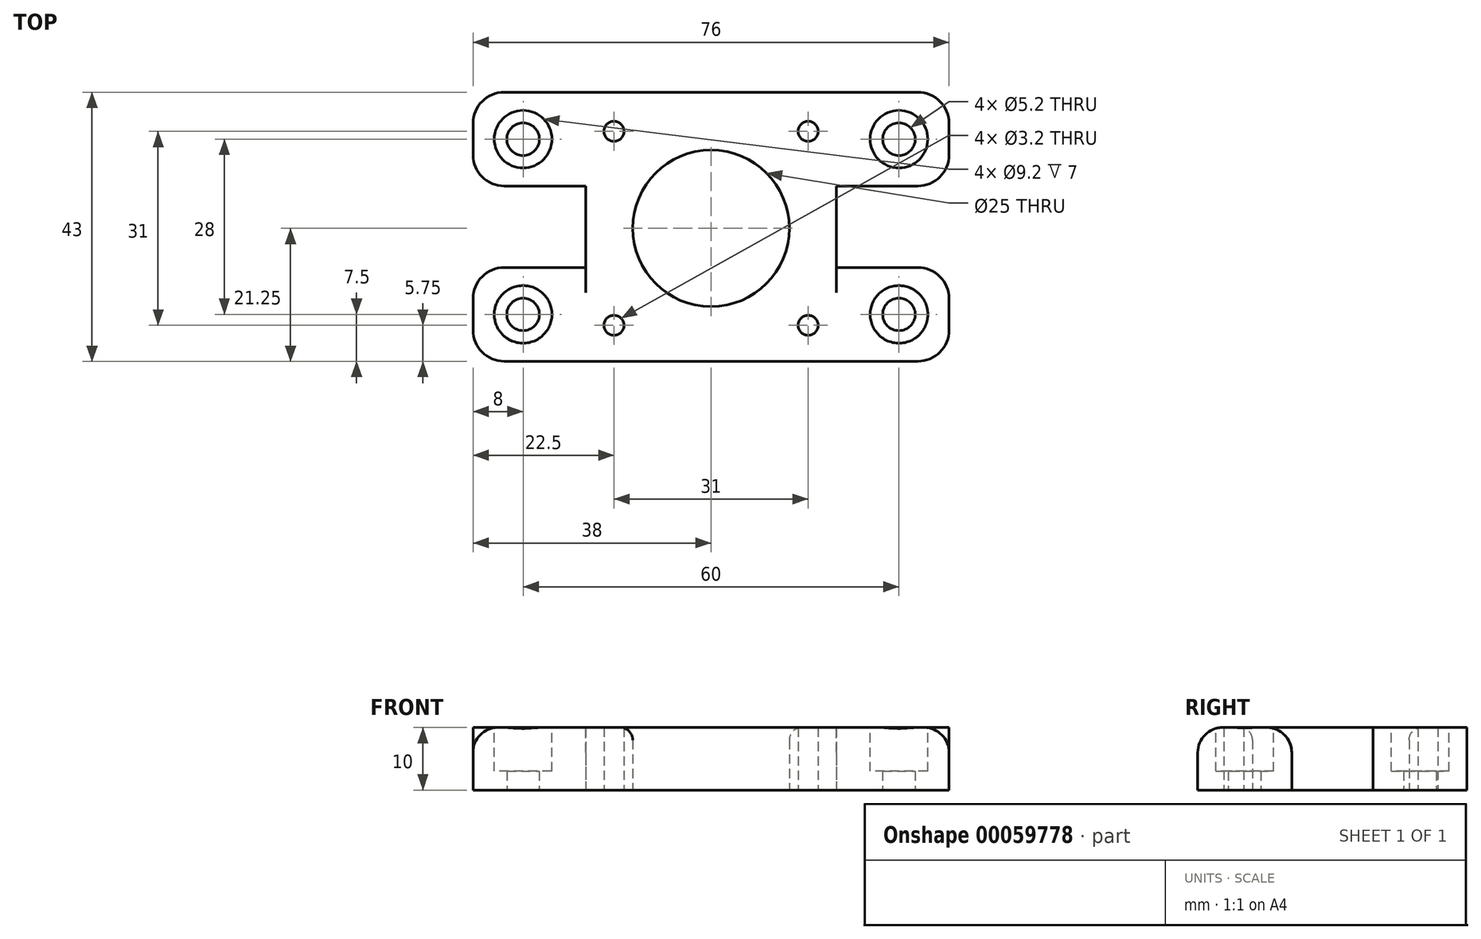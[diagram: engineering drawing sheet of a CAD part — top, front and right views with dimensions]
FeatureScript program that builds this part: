
annotation { "Feature Type Name" : "Feature", "Feature Type Description" : "" }
export const myFeature = defineFeature(function(context is Context, id is Id, definition is map)
    precondition{}
    {
        {
            assignVariable(context, id + "F0", {"name" : "defaultThickness", "anyValue" : 10 * mm});
        }
        {
            var Q0;
            Q0=qCreatedBy(makeId("Top.planeOp"),FACE);
            var sketch = newSketch(context, id + "F1", { "sketchPlane" : qUnion([Q0])});
            skLineSegment(sketch, "E0.rect.bottom", {"start": v(-20, 21.5) * mm, "end": v(20, 21.5) * mm});
            skLineSegment(sketch, "E0.rect.top", {"start": v(-20, -21.5) * mm, "end": v(20, -21.5) * mm});
            skLineSegment(sketch, "E0.rect.left", {"start": v(-20, 21.5) * mm, "end": v(-20, -21.5) * mm});
            skLineSegment(sketch, "E0.rect.right", {"start": v(20, 21.5) * mm, "end": v(20, -21.5) * mm});
            skPoint(sketch, "E0.rect.middle", {"position": v(0, 0) * mm});
            skLineSegment(sketch, "E1", {"start": v(0, 21.5) * mm, "end": v(0, 0) * mm, "construction": true});
            skLineSegment(sketch, "E2", {"start": v(0, -21.5) * mm, "end": v(0, 0) * mm, "construction": true});
            skSolve(sketch);
        }
        {
            var Q0;
            Q0=qSketchRegion(id+"F1",true);
            extrude(context, id + "F2", {"entities" : qUnion([Q0]), "depth" : getVariable(context, 'defaultThickness')});
        }
        {
            var Q0;
            Q0=makeQuery(id+"F2.opExtrude","CAP_FACE",FACE,{"disambiguationData":[OSD([sQuery(id+"F1.wireOp",EDGE,"E0.rect.bottom"),sQuery(id+"F1.wireOp",EDGE,"E0.rect.top"),sQuery(id+"F1.wireOp",EDGE,"E0.rect.left"),sQuery(id+"F1.wireOp",EDGE,"E0.rect.right"),sQuery(id+"F1.wireOp",EDGE,"f753b575-aba3-41a6-833e-e4f93ea5e4c448.MirrorCS"),sQuery(id+"F1.wireOp",EDGE,"f753b575-aba3-41a6-833e-e4f93ea5e4c449.MirrorC"),sQuery(id+"F1.wireOp",EDGE,"f753b575-aba3-41a6-833e-e4f93ea5e4c450.MirrorCS"),sQuery(id+"F1.wireOp",EDGE,"f753b575-aba3-41a6-833e-e4f93ea5e4c451.MirrorCS"),sQuery(id+"F1.wireOp",EDGE,"bc571038-01dd-487e-b9a0-def5901bd9830.MirrorCS"),sQuery(id+"F1.wireOp",EDGE,"12bf195a-cfe4-4b15-ab7f-3f731c2d51660.MirrorCS"),sQuery(id+"F1.wireOp",EDGE,"455051b4-7426-46a8-a129-8b9c592178470.MirrorCS"),sQuery(id+"F1.wireOp",EDGE,"7dd5bb44-a427-4bdb-ba85-5ced25b216bb0.MirrorC")])],"isStart":true});
            var sketch = newSketch(context, id + "F3", { "sketchPlane" : qUnion([Q0])});
            skLineSegment(sketch, "E3", {"start": v(20, -21.5) * mm, "end": v(20, -21.5) * mm});
            skLineSegment(sketch, "E4", {"start": v(20, -21.5) * mm, "end": v(-20, -21.5) * mm, "construction": true});
            skLineSegment(sketch, "E5", {"start": v(-20, -21.5) * mm, "end": v(-20, -21.5) * mm});
            skLineSegment(sketch, "E6", {"start": v(0, 21.5) * mm, "end": v(0, 0) * mm, "construction": true});
            skLineSegment(sketch, "E7", {"start": v(0, 0) * mm, "end": v(0, -21) * mm, "construction": true});
            skLineSegment(sketch, "E8", {"start": v(0, -21) * mm, "end": v(-20, -21) * mm, "construction": true});
            skLineSegment(sketch, "E9", {"start": v(-20, -21) * mm, "end": v(-20, 21.5) * mm, "construction": true});
            skLineSegment(sketch, "E10", {"start": v(-20, 21.5) * mm, "end": v(0, 21.5) * mm, "construction": true});
            skLineSegment(sketch, "E11", {"start": v(20, 21.5) * mm, "end": v(20, -21) * mm, "construction": true});
            skLineSegment(sketch, "E12", {"start": v(20, -21) * mm, "end": v(0, -21) * mm, "construction": true});
            skLineSegment(sketch, "E13", {"start": v(-20, 0.25) * mm, "end": v(0, 0.25) * mm, "construction": true});
            skLineSegment(sketch, "E14", {"start": v(0, 0.25) * mm, "end": v(20, 0.25) * mm, "construction": true});
            skPoint(sketch, "E15", {"position": v(0, 0.25) * mm});
            skCircle(sketch, "E16", {"center": v(0, 0.25) * mm, "radius": 12.5 * mm});
            skCircle(sketch, "E17", {"center": v(-15.5, -15.25) * mm, "radius": 1.6 * mm});
            skCircle(sketch, "E18", {"center": v(15.5, -15.25) * mm, "radius": 1.6 * mm});
            skCircle(sketch, "E19", {"center": v(15.5, 15.75) * mm, "radius": 1.6 * mm});
            skCircle(sketch, "E20", {"center": v(-15.5, 15.75) * mm, "radius": 1.6 * mm});
            skSolve(sketch);
        }
        {
            var Q0;
            Q0=qSketchRegion(id+"F3",true);
            extrude(context, id + "F4", {"entities" : qUnion([Q0]), "operationType" : NewBodyOperationType.REMOVE, "endBound" : BoundingType.THROUGH_ALL, "oppositeDirection" : true, "depth" : 25 * mm});
        }
        {
            var Q0;
            Q0=makeQuery(id+"F2.opExtrude","CAP_FACE",FACE,{"disambiguationData":[OSD([sQuery(id+"F1.wireOp",EDGE,"E0.rect.bottom"),sQuery(id+"F1.wireOp",EDGE,"E0.rect.top"),sQuery(id+"F1.wireOp",EDGE,"E0.rect.left"),sQuery(id+"F1.wireOp",EDGE,"E0.rect.right")])],"isStart":true});
            var sketch = newSketch(context, id + "F5", { "sketchPlane" : qUnion([Q0])});
            skLineSegment(sketch, "E21", {"start": v(-20, 21.5) * mm, "end": v(-38, 21.5) * mm});
            skLineSegment(sketch, "E22", {"start": v(-38, 21.5) * mm, "end": v(-38, 6.5) * mm});
            skLineSegment(sketch, "E23", {"start": v(-38, 6.5) * mm, "end": v(-20, 6.5) * mm});
            skLineSegment(sketch, "E24", {"start": v(-20, 21.5) * mm, "end": v(-20, 6.5) * mm});
            skCircle(sketch, "E25", {"center": v(-30, 14) * mm, "radius": 2.6 * mm});
            skLineSegment(sketch, "E26.MirrorCS", {"start": v(20, 21.5) * mm, "end": v(38, 21.5) * mm});
            skLineSegment(sketch, "E27.MirrorCS", {"start": v(38, 6.5) * mm, "end": v(20, 6.5) * mm});
            skCircle(sketch, "E28.MirrorC", {"center": v(30, 14) * mm, "radius": 2.6 * mm});
            skLineSegment(sketch, "E29.MirrorCS", {"start": v(20, 21.5) * mm, "end": v(20, 6.5) * mm});
            skLineSegment(sketch, "E30.MirrorCS", {"start": v(38, 21.5) * mm, "end": v(38, 6.5) * mm});
            skLineSegment(sketch, "E31", {"start": v(-20, -21.5) * mm, "end": v(-38, -21.5) * mm});
            skLineSegment(sketch, "E32", {"start": v(-38, -21.5) * mm, "end": v(-38, -6.5) * mm});
            skLineSegment(sketch, "E33", {"start": v(-38, -6.5) * mm, "end": v(-20, -6.5) * mm});
            skLineSegment(sketch, "E34", {"start": v(-20, -6.5) * mm, "end": v(-20, -21.5) * mm});
            skLineSegment(sketch, "E35.bottom", {"start": v(20, -21.5) * mm, "end": v(38, -21.5) * mm});
            skLineSegment(sketch, "E35.top", {"start": v(20, -6.5) * mm, "end": v(38, -6.5) * mm});
            skLineSegment(sketch, "E35.left", {"start": v(20, -21.5) * mm, "end": v(20, -6.5) * mm});
            skLineSegment(sketch, "E35.right", {"start": v(38, -21.5) * mm, "end": v(38, -6.5) * mm});
            skCircle(sketch, "E36", {"center": v(-30, -14) * mm, "radius": 2.6 * mm});
            skCircle(sketch, "E37", {"center": v(30, -14) * mm, "radius": 2.6 * mm});
            skSolve(sketch);
        }
        {
            var Q0;
            Q0=qSketchRegion(id+"F5",true);
            extrude(context, id + "F6", {"entities" : qUnion([Q0]), "operationType" : NewBodyOperationType.ADD, "oppositeDirection" : true, "depth" : getVariable(context, 'defaultThickness')});
        }
        {
            var Q0;
            Q0=makeQuery(id+"F2.opExtrude","SWEPT_EDGE",EDGE,{"disambiguationData":[OSD([sQuery(id+"F1.wireOp",EDGE,"f753b575-aba3-41a6-833e-e4f93ea5e4c450.MirrorCS"),sQuery(id+"F1.wireOp",EDGE,"f753b575-aba3-41a6-833e-e4f93ea5e4c451.MirrorCS")])]});
            var Q1;
            Q1=makeQuery(id+"F2.opExtrude","SWEPT_EDGE",EDGE,{"disambiguationData":[OSD([sQuery(id+"F1.wireOp",EDGE,"f753b575-aba3-41a6-833e-e4f93ea5e4c448.MirrorCS"),sQuery(id+"F1.wireOp",EDGE,"f753b575-aba3-41a6-833e-e4f93ea5e4c451.MirrorCS")])]});
            var Q2;
            Q2=makeQuery(id+"F2.opExtrude","SWEPT_EDGE",EDGE,{"disambiguationData":[OSD([sQuery(id+"F1.wireOp",EDGE,"12bf195a-cfe4-4b15-ab7f-3f731c2d51660.MirrorCS"),sQuery(id+"F1.wireOp",EDGE,"455051b4-7426-46a8-a129-8b9c592178470.MirrorCS")])]});
            var Q3;
            Q3=makeQuery(id+"F2.opExtrude","SWEPT_EDGE",EDGE,{"disambiguationData":[OSD([sQuery(id+"F1.wireOp",EDGE,"bc571038-01dd-487e-b9a0-def5901bd9830.MirrorCS"),sQuery(id+"F1.wireOp",EDGE,"12bf195a-cfe4-4b15-ab7f-3f731c2d51660.MirrorCS")])]});
            var Q4;
            Q4=makeQuery(id+"F1IgwxVWLGXEZ05_1.opExtrude","CAP_EDGE",EDGE,{"disambiguationData":[OSD([sQuery(id+"F46VJo8EH1OxCCN_1.wireOp",EDGE,"a8bc6f70-3fce-4169-98be-ded91195f1be.right")])],"isStart":false});
            var Q5;
            Q5=makeQuery(id+"F1IgwxVWLGXEZ05_1.opExtrude","CAP_EDGE",EDGE,{"disambiguationData":[OSD([sQuery(id+"F46VJo8EH1OxCCN_1.wireOp",EDGE,"a8bc6f70-3fce-4169-98be-ded91195f1be.left")])],"isStart":false});
            var Q6;
            Q6=makeQuery(id+"F6.opExtrude","SWEPT_EDGE",EDGE,{"disambiguationData":[OSD([sQuery(id+"F5.wireOp",EDGE,"E26.MirrorCS"),sQuery(id+"F5.wireOp",EDGE,"E30.MirrorCS")])]});
            var Q7;
            Q7=makeQuery(id+"F6.opExtrude","SWEPT_EDGE",EDGE,{"disambiguationData":[OSD([sQuery(id+"F5.wireOp",EDGE,"E27.MirrorCS"),sQuery(id+"F5.wireOp",EDGE,"E30.MirrorCS")])]});
            var Q8;
            Q8=makeQuery(id+"F6.opExtrude","SWEPT_EDGE",EDGE,{"disambiguationData":[OSD([sQuery(id+"F5.wireOp",EDGE,"E22"),sQuery(id+"F5.wireOp",EDGE,"E23")])]});
            var Q9;
            Q9=makeQuery(id+"F6.opExtrude","SWEPT_EDGE",EDGE,{"disambiguationData":[OSD([sQuery(id+"F5.wireOp",EDGE,"E21"),sQuery(id+"F5.wireOp",EDGE,"E22")])]});
            var Q10;
            Q10=makeQuery(id+"F6.opExtrude","SWEPT_EDGE",EDGE,{"disambiguationData":[OSD([sQuery(id+"F5.wireOp",EDGE,"E32"),sQuery(id+"F5.wireOp",EDGE,"E33")])]});
            var Q11;
            Q11=makeQuery(id+"F6.opExtrude","SWEPT_EDGE",EDGE,{"disambiguationData":[OSD([sQuery(id+"F5.wireOp",EDGE,"E31"),sQuery(id+"F5.wireOp",EDGE,"E32")])]});
            var Q12;
            Q12=makeQuery(id+"F6.opExtrude","SWEPT_EDGE",EDGE,{"disambiguationData":[OSD([sQuery(id+"F5.wireOp",EDGE,"E35.top"),sQuery(id+"F5.wireOp",EDGE,"E35.right")])]});
            var Q13;
            Q13=makeQuery(id+"F6.opExtrude","SWEPT_EDGE",EDGE,{"disambiguationData":[OSD([sQuery(id+"F5.wireOp",EDGE,"E35.bottom"),sQuery(id+"F5.wireOp",EDGE,"E35.right")])]});
            var Q14;
            Q14=makeQuery(id+"F6.opExtrude","SWEPT_EDGE",EDGE,{"disambiguationData":[OSD([sQuery(id+"F1.wireOp",EDGE,"E0.rect.right"),sQuery(id+"F5.wireOp",EDGE,"E35.top"),sQuery(id+"F5.wireOp",EDGE,"E35.left")])]});
            var Q15;
            Q15=makeQuery(id+"F6.opExtrude","SWEPT_EDGE",EDGE,{"disambiguationData":[OSD([sQuery(id+"F1.wireOp",EDGE,"E0.rect.right"),sQuery(id+"F5.wireOp",EDGE,"E27.MirrorCS"),sQuery(id+"F5.wireOp",EDGE,"E29.MirrorCS")])]});
            var Q16;
            Q16=makeQuery(id+"F6.opExtrude","SWEPT_EDGE",EDGE,{"disambiguationData":[OSD([sQuery(id+"F1.wireOp",EDGE,"E0.rect.left"),sQuery(id+"F5.wireOp",EDGE,"E33"),sQuery(id+"F5.wireOp",EDGE,"E34")])]});
            var Q17;
            Q17=makeQuery(id+"F6.opExtrude","SWEPT_EDGE",EDGE,{"disambiguationData":[OSD([sQuery(id+"F1.wireOp",EDGE,"E0.rect.left"),sQuery(id+"F5.wireOp",EDGE,"E23"),sQuery(id+"F5.wireOp",EDGE,"E24")])]});
            fillet(context, id + "F7", {"entities" : qUnion([Q0, Q1, Q2, Q3, Q4, Q5, Q6, Q7, Q8, Q9, Q10, Q11, Q12, Q13, Q14, Q15, Q16, Q17]), "radius" : 5 * mm, "tangentPropagation" : true, "allowEdgeOverflow" : false});
        }
        {
            var Q0;
            Q0=makeQuery(id+"F6.boolean.opBoolean","MERGE",FACE,{"derivedFrom":[makeQuery(id+"F2.opExtrude","CAP_FACE",FACE,{"disambiguationData":[OSD([sQuery(id+"F1.wireOp",EDGE,"E0.rect.bottom"),sQuery(id+"F1.wireOp",EDGE,"E0.rect.top"),sQuery(id+"F1.wireOp",EDGE,"E0.rect.left"),sQuery(id+"F1.wireOp",EDGE,"E0.rect.right")])],"isStart":false}),makeQuery(id+"F6.opExtrude","CAP_FACE",FACE,{"disambiguationData":[OSD([sQuery(id+"F5.wireOp",EDGE,"E21"),sQuery(id+"F5.wireOp",EDGE,"E22"),sQuery(id+"F5.wireOp",EDGE,"E23"),sQuery(id+"F5.wireOp",EDGE,"E24"),sQuery(id+"F5.wireOp",EDGE,"E25")])],"isStart":false}),makeQuery(id+"F6.opExtrude","CAP_FACE",FACE,{"disambiguationData":[OSD([sQuery(id+"F5.wireOp",EDGE,"E26.MirrorCS"),sQuery(id+"F5.wireOp",EDGE,"E27.MirrorCS"),sQuery(id+"F5.wireOp",EDGE,"E28.MirrorC"),sQuery(id+"F5.wireOp",EDGE,"E29.MirrorCS"),sQuery(id+"F5.wireOp",EDGE,"E30.MirrorCS")])],"isStart":false}),makeQuery(id+"F6.opExtrude","CAP_FACE",FACE,{"disambiguationData":[OSD([sQuery(id+"F5.wireOp",EDGE,"E31"),sQuery(id+"F5.wireOp",EDGE,"E32"),sQuery(id+"F5.wireOp",EDGE,"E33"),sQuery(id+"F5.wireOp",EDGE,"E34"),sQuery(id+"F5.wireOp",EDGE,"E36")])],"isStart":false}),makeQuery(id+"F6.opExtrude","CAP_FACE",FACE,{"disambiguationData":[OSD([sQuery(id+"F5.wireOp",EDGE,"E35.bottom"),sQuery(id+"F5.wireOp",EDGE,"E35.top"),sQuery(id+"F5.wireOp",EDGE,"E35.left"),sQuery(id+"F5.wireOp",EDGE,"E35.right"),sQuery(id+"F5.wireOp",EDGE,"E37")])],"isStart":false})]});
            var sketch = newSketch(context, id + "F8", { "sketchPlane" : qUnion([Q0])});
            skCircle(sketch, "E38", {"center": v(-30, 14) * mm, "radius": 4.6 * mm});
            skCircle(sketch, "E39", {"center": v(30, 14) * mm, "radius": 4.6 * mm});
            skCircle(sketch, "E40", {"center": v(-30, -14) * mm, "radius": 4.6 * mm});
            skCircle(sketch, "E41", {"center": v(30, -14) * mm, "radius": 4.6 * mm});
            skSolve(sketch);
        }
        {
            var Q0;
            Q0=makeQuery(id+"F8.imprint","IMPRINT",FACE,{"disambiguationData":[TD([[makeQuery(id+"F8.imprint","IMPRINT",EDGE,{"derivedFrom":sQuery(id+"F8.wireOp",EDGE,"E38")}),1.0]])]});
            var Q1;
            Q1=makeQuery(id+"F8.imprint","IMPRINT",FACE,{"disambiguationData":[TD([[makeQuery(id+"F8.imprint","IMPRINT",EDGE,{"derivedFrom":sQuery(id+"F8.wireOp",EDGE,"E40")}),1.0]])]});
            var Q2;
            Q2=makeQuery(id+"F8.imprint","IMPRINT",FACE,{"disambiguationData":[TD([[makeQuery(id+"F8.imprint","IMPRINT",EDGE,{"derivedFrom":sQuery(id+"F8.wireOp",EDGE,"E39")}),1.0]])]});
            var Q3;
            Q3=makeQuery(id+"F8.imprint","IMPRINT",FACE,{"disambiguationData":[TD([[makeQuery(id+"F8.imprint","IMPRINT",EDGE,{"derivedFrom":sQuery(id+"F8.wireOp",EDGE,"E41")}),1.0]])]});
            extrude(context, id + "F9", {"entities" : qUnion([Q0, Q1, Q2, Q3]), "operationType" : NewBodyOperationType.REMOVE, "oppositeDirection" : true, "depth" : 7 * mm});
        }
        {
            var Q0;
            Q0=makeQuery(id+"F9.boolean.opBoolean","COPY",EDGE,{"derivedFrom":makeQuery(id+"F9.opExtrude","CAP_EDGE",EDGE,{"disambiguationData":[OSD([sQuery(id+"F8.wireOp",EDGE,"E39")])],"isStart":true})});
            var Q1;
            Q1=makeQuery(id+"F9.boolean.opBoolean","COPY",EDGE,{"derivedFrom":makeQuery(id+"F9.opExtrude","CAP_EDGE",EDGE,{"disambiguationData":[OSD([sQuery(id+"F8.wireOp",EDGE,"E38")])],"isStart":true})});
            var Q2;
            Q2=makeQuery(id+"F9.boolean.opBoolean","COPY",EDGE,{"derivedFrom":makeQuery(id+"F9.opExtrude","CAP_EDGE",EDGE,{"disambiguationData":[OSD([sQuery(id+"F8.wireOp",EDGE,"E40")])],"isStart":true})});
            var Q3;
            Q3=makeQuery(id+"F9.boolean.opBoolean","COPY",EDGE,{"derivedFrom":makeQuery(id+"F9.opExtrude","CAP_EDGE",EDGE,{"disambiguationData":[OSD([sQuery(id+"F8.wireOp",EDGE,"E41")])],"isStart":true})});
            var Q4;
            Q4=makeQuery(id+"F6.boolean.opBoolean","MERGE",EDGE,{"derivedFrom":[makeQuery(id+"F2.opExtrude","CAP_EDGE",EDGE,{"disambiguationData":[OSD([sQuery(id+"F1.wireOp",EDGE,"E0.rect.top")])],"isStart":false}),makeQuery(id+"F6.opExtrude","CAP_EDGE",EDGE,{"disambiguationData":[OSD([sQuery(id+"F5.wireOp",EDGE,"E21")])],"isStart":false}),makeQuery(id+"F6.opExtrude","CAP_EDGE",EDGE,{"disambiguationData":[OSD([sQuery(id+"F5.wireOp",EDGE,"E26.MirrorCS")])],"isStart":false})]});
            fillet(context, id + "F10", {"entities" : qUnion([Q0, Q1, Q2, Q3, Q4]), "radius" : 4 * mm, "tangentPropagation" : true, "allowEdgeOverflow" : false});
        }
        {
            var Q0;
            Q0=makeQuery(id+"F4.boolean.opBoolean","INTERSECT",EDGE,{"derivedFrom":[makeQuery(id+"F2.opExtrude","CAP_FACE",FACE,{"disambiguationData":[OSD([sQuery(id+"F1.wireOp",EDGE,"E0.rect.bottom"),sQuery(id+"F1.wireOp",EDGE,"E0.rect.top"),sQuery(id+"F1.wireOp",EDGE,"E0.rect.left"),sQuery(id+"F1.wireOp",EDGE,"E0.rect.right")])],"isStart":false}),makeQuery(id+"F4.opExtrude","SWEPT_FACE",FACE,{"disambiguationData":[OSD([sQuery(id+"F3.wireOp",EDGE,"E16")])]})]});
            fillet(context, id + "F11", {"entities" : qUnion([Q0]), "radius" : 2 * mm, "tangentPropagation" : true, "allowEdgeOverflow" : false});
        }
    });
